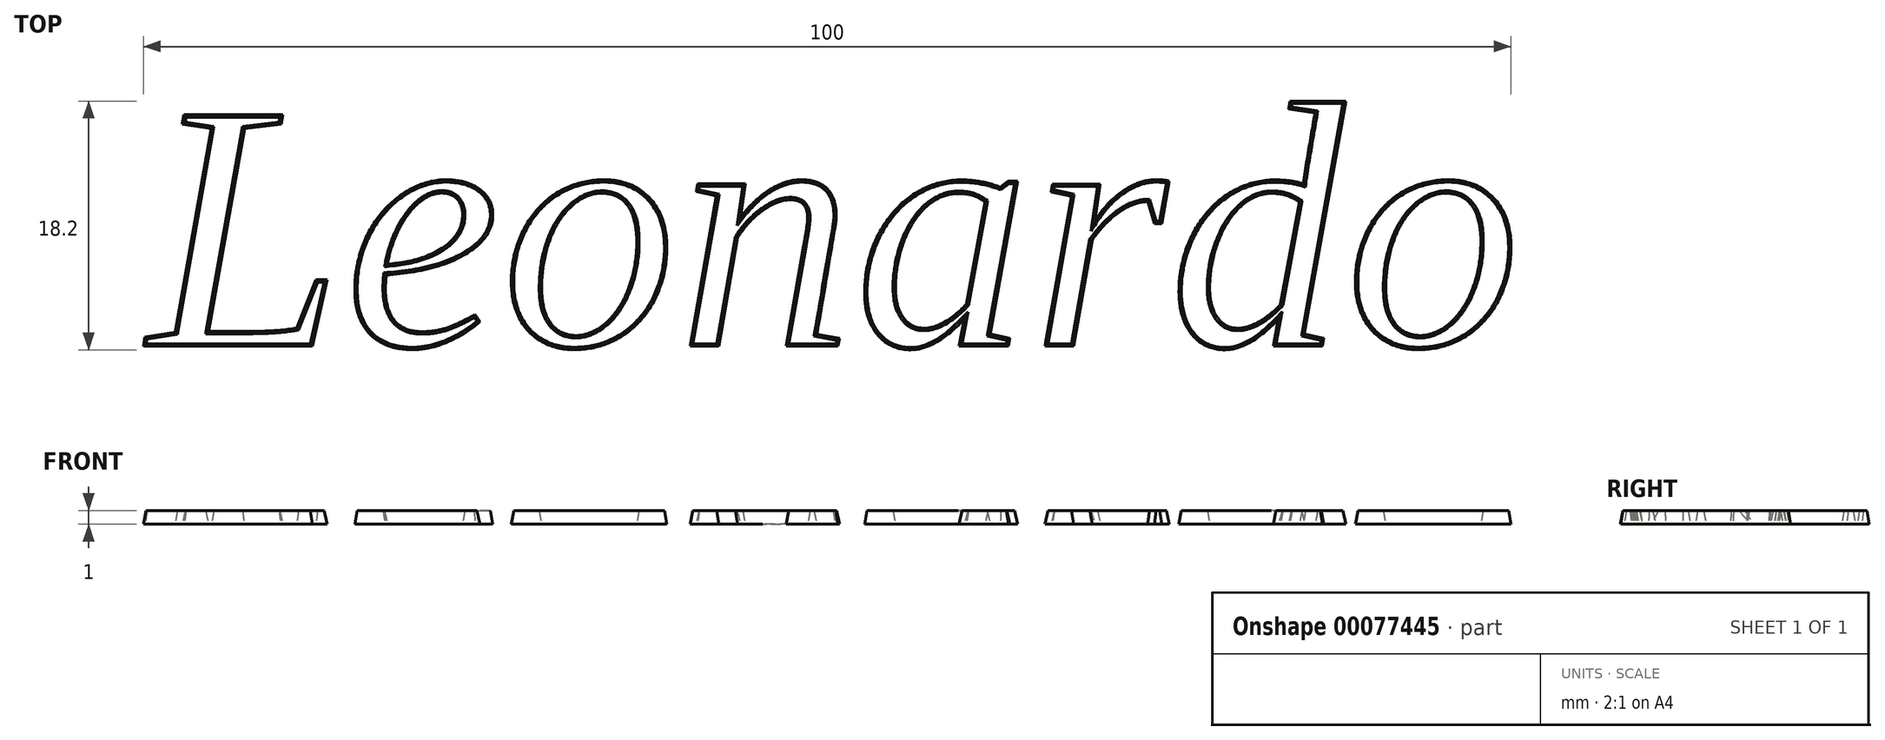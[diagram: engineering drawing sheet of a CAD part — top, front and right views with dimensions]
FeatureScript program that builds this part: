
annotation { "Feature Type Name" : "Feature", "Feature Type Description" : "" }
export const myFeature = defineFeature(function(context is Context, id is Id, definition is map)
    precondition{}
    {
        {
            var Q0;
            Q0=qCreatedBy(makeId("Top.planeOp"),FACE);
            var sketch = newSketch(context, id + "F0", { "sketchPlane" : qUnion([Q0])});
            skText(sketch, "E0", { "text": "Leonardo", "fontName": "Tinos-Italic.ttf"});
            const initialGuessF0  = {"E0": [0.03076, -0.00874, 1, 0, 0.0186]};
            skSetInitialGuess(sketch, initialGuessF0);
            skSolve(sketch);
        }
        {
            var Q0;
            Q0=makeQuery(id+"F0.imprint","IMPRINT",FACE,{"disambiguationData":[TD([[makeQuery(id+"F0.imprint","IMPRINT",EDGE,{"derivedFrom":sQuery(id+"F0.wireOp",EDGE,"E0.sketch_text.stroke-0")}),-1.0]])]});
            var Q1;
            Q1=makeQuery(id+"F0.imprint","IMPRINT",FACE,{"disambiguationData":[TD([[makeQuery(id+"F0.imprint","IMPRINT",EDGE,{"derivedFrom":sQuery(id+"F0.wireOp",EDGE,"E0.sketch_text.stroke-15")}),-1.0]])]});
            var Q2;
            Q2=makeQuery(id+"F0.imprint","IMPRINT",FACE,{"disambiguationData":[TD([[makeQuery(id+"F0.imprint","IMPRINT",EDGE,{"derivedFrom":sQuery(id+"F0.wireOp",EDGE,"E0.sketch_text.stroke-39")}),-1.0]])]});
            var Q3;
            Q3=makeQuery(id+"F0.imprint","IMPRINT",FACE,{"disambiguationData":[TD([[makeQuery(id+"F0.imprint","IMPRINT",EDGE,{"derivedFrom":sQuery(id+"F0.wireOp",EDGE,"E0.sketch_text.stroke-59")}),-1.0]])]});
            var Q4;
            Q4=makeQuery(id+"F0.imprint","IMPRINT",FACE,{"disambiguationData":[TD([[makeQuery(id+"F0.imprint","IMPRINT",EDGE,{"derivedFrom":sQuery(id+"F0.wireOp",EDGE,"E0.sketch_text.stroke-81")}),-1.0]])]});
            var Q5;
            Q5=makeQuery(id+"F0.imprint","IMPRINT",FACE,{"disambiguationData":[TD([[makeQuery(id+"F0.imprint","IMPRINT",EDGE,{"derivedFrom":sQuery(id+"F0.wireOp",EDGE,"E0.sketch_text.stroke-104")}),-1.0]])]});
            var Q6;
            Q6=makeQuery(id+"F0.imprint","IMPRINT",FACE,{"disambiguationData":[TD([[makeQuery(id+"F0.imprint","IMPRINT",EDGE,{"derivedFrom":sQuery(id+"F0.wireOp",EDGE,"E0.sketch_text.stroke-119")}),-1.0]])]});
            var Q7;
            Q7=makeQuery(id+"F0.imprint","IMPRINT",FACE,{"disambiguationData":[TD([[makeQuery(id+"F0.imprint","IMPRINT",EDGE,{"derivedFrom":sQuery(id+"F0.wireOp",EDGE,"E0.sketch_text.stroke-145")}),-1.0]])]});
            extrude(context, id + "F1", {"entities" : qUnion([Q0, Q1, Q2, Q3, Q4, Q5, Q6, Q7]), "depth" : 1 * mm, "hasDraft" : true, "draftAngle" : 10 * degree, "draftPullDirection" : true});
        }
    });
